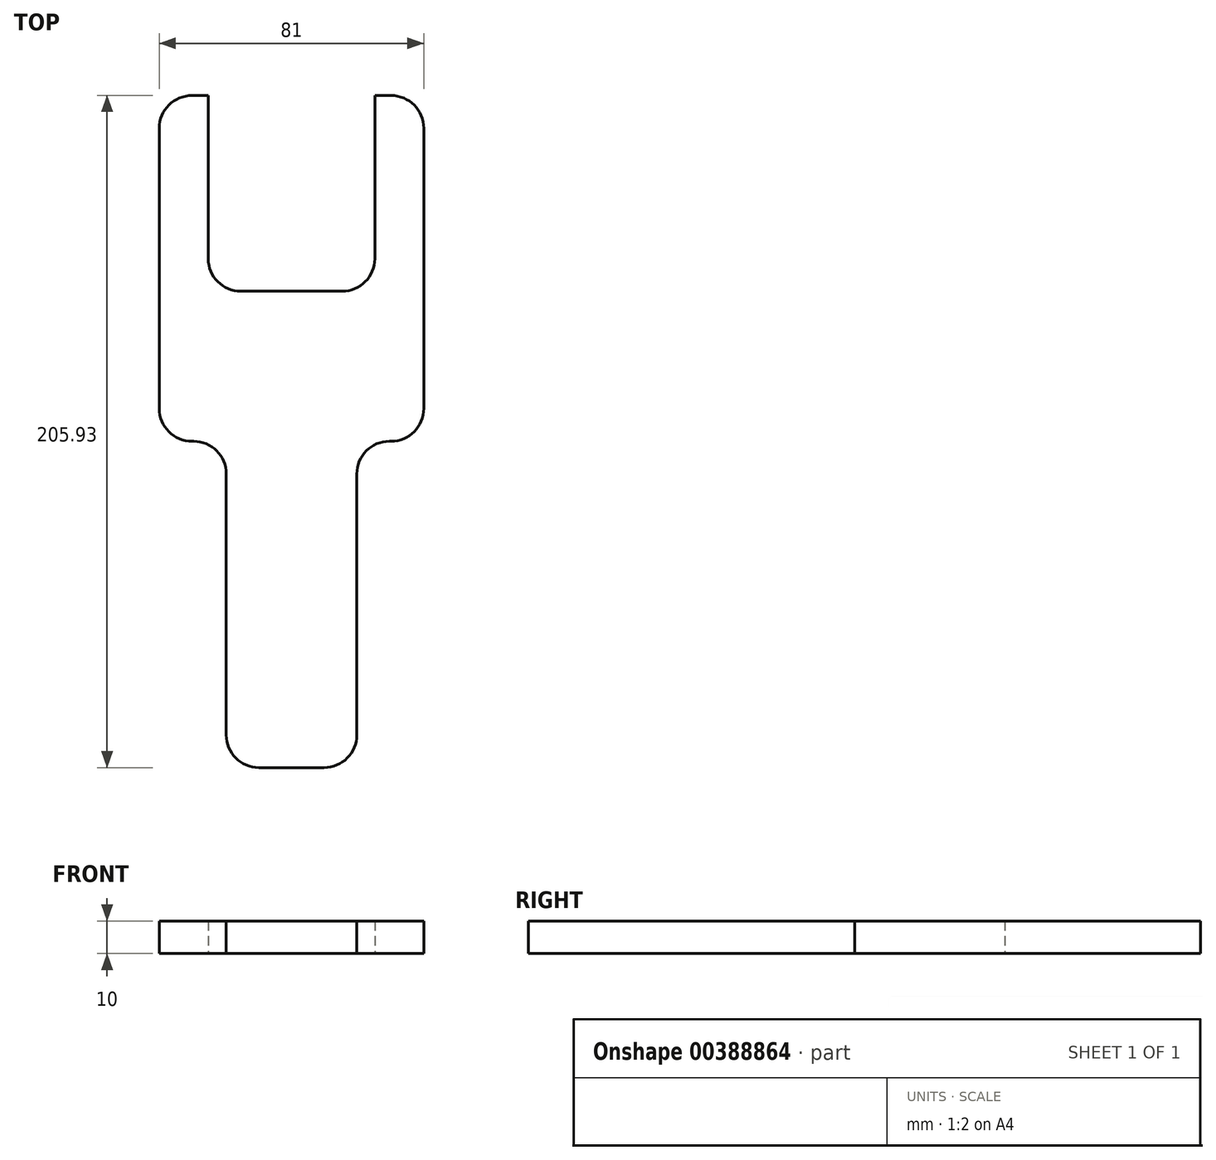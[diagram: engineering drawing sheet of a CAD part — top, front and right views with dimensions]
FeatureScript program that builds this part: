
annotation { "Feature Type Name" : "Feature", "Feature Type Description" : "" }
export const myFeature = defineFeature(function(context is Context, id is Id, definition is map)
    precondition{}
    {
        {
            var Q0;
            Q0=qCreatedBy(makeId("Top.planeOp"),FACE);
            var sketch = newSketch(context, id + "F0", { "sketchPlane" : qUnion([Q0])});
            skLineSegment(sketch, "E0", {"start": v(0, 87.3) * mm, "end": v(0, -159.9) * mm, "construction": true});
            skLineSegment(sketch, "E1", {"start": v(69.17, 0) * mm, "end": v(-67.83, 0) * mm, "construction": true});
            skLineSegment(sketch, "E2", {"start": v(25.5, 60) * mm, "end": v(25.5, 0) * mm});
            skLineSegment(sketch, "E3", {"start": v(25.5, 0) * mm, "end": v(0, 0) * mm});
            skLineSegment(sketch, "E4", {"start": v(25.5, 60) * mm, "end": v(40.5, 60) * mm});
            skLineSegment(sketch, "E5", {"start": v(40.5, 60) * mm, "end": v(40.5, -45.93) * mm});
            skLineSegment(sketch, "E6", {"start": v(40.5, -45.93) * mm, "end": v(20, -45.93) * mm});
            skLineSegment(sketch, "E7", {"start": v(20, -45.93) * mm, "end": v(20, -145.93) * mm});
            skLineSegment(sketch, "E8", {"start": v(20, -145.93) * mm, "end": v(0, -145.93) * mm});
            skLineSegment(sketch, "E9.MirrorCS", {"start": v(-25.5, 0) * mm, "end": v(0, 0) * mm});
            skLineSegment(sketch, "E10.MirrorCS", {"start": v(-25.5, 60) * mm, "end": v(-25.5, 0) * mm});
            skLineSegment(sketch, "E11.MirrorCS", {"start": v(-40.5, 60) * mm, "end": v(-40.5, -45.93) * mm});
            skLineSegment(sketch, "E12.MirrorCS", {"start": v(-40.5, -45.93) * mm, "end": v(-20, -45.93) * mm});
            skLineSegment(sketch, "E13.MirrorCS", {"start": v(-20, -45.93) * mm, "end": v(-20, -145.93) * mm});
            skLineSegment(sketch, "E14.MirrorCS", {"start": v(-20, -145.93) * mm, "end": v(0, -145.93) * mm});
            skLineSegment(sketch, "E15.MirrorCS", {"start": v(-25.5, 60) * mm, "end": v(-40.5, 60) * mm});
            skSolve(sketch);
        }
        {
            var Q0;
            Q0 = qSketchRegion(id + "F0", true);
            extrude(context, id + "F1", {"entities" : qUnion([Q0]), "depth" : 10 * mm});
        }
        {
            var Q0;
            Q0=makeQuery(id+"F1.opExtrude","SWEPT_EDGE",EDGE,{"disambiguationData":[OSD([sQuery(id+"F0.wireOp",EDGE,"E7"),sQuery(id+"F0.wireOp",EDGE,"E8")])]});
            var Q1;
            Q1=makeQuery(id+"F1.opExtrude","SWEPT_EDGE",EDGE,{"disambiguationData":[OSD([sQuery(id+"F0.wireOp",EDGE,"E13.MirrorCS"),sQuery(id+"F0.wireOp",EDGE,"E14.MirrorCS")])]});
            var Q2;
            Q2=makeQuery(id+"F1.opExtrude","SWEPT_EDGE",EDGE,{"disambiguationData":[OSD([sQuery(id+"F0.wireOp",EDGE,"E5"),sQuery(id+"F0.wireOp",EDGE,"E6")])]});
            var Q3;
            Q3=makeQuery(id+"F1.opExtrude","SWEPT_EDGE",EDGE,{"disambiguationData":[OSD([sQuery(id+"F0.wireOp",EDGE,"E6"),sQuery(id+"F0.wireOp",EDGE,"E7")])]});
            var Q4;
            Q4=makeQuery(id+"F1.opExtrude","SWEPT_EDGE",EDGE,{"disambiguationData":[OSD([sQuery(id+"F0.wireOp",EDGE,"E11.MirrorCS"),sQuery(id+"F0.wireOp",EDGE,"E12.MirrorCS")])]});
            var Q5;
            Q5=makeQuery(id+"F1.opExtrude","SWEPT_EDGE",EDGE,{"disambiguationData":[OSD([sQuery(id+"F0.wireOp",EDGE,"E12.MirrorCS"),sQuery(id+"F0.wireOp",EDGE,"E13.MirrorCS")])]});
            var Q6;
            Q6=makeQuery(id+"F1.opExtrude","SWEPT_EDGE",EDGE,{"disambiguationData":[OSD([sQuery(id+"F0.wireOp",EDGE,"E2"),sQuery(id+"F0.wireOp",EDGE,"E3")])]});
            var Q7;
            Q7=makeQuery(id+"F1.opExtrude","SWEPT_EDGE",EDGE,{"disambiguationData":[OSD([sQuery(id+"F0.wireOp",EDGE,"E9.MirrorCS"),sQuery(id+"F0.wireOp",EDGE,"E10.MirrorCS")])]});
            var Q8;
            Q8=makeQuery(id+"F1.opExtrude","SWEPT_EDGE",EDGE,{"disambiguationData":[OSD([sQuery(id+"F0.wireOp",EDGE,"E4"),sQuery(id+"F0.wireOp",EDGE,"E5")])]});
            var Q9;
            Q9=makeQuery(id+"F1.opExtrude","SWEPT_EDGE",EDGE,{"disambiguationData":[OSD([sQuery(id+"F0.wireOp",EDGE,"E11.MirrorCS"),sQuery(id+"F0.wireOp",EDGE,"E15.MirrorCS")])]});
            fillet(context, id + "F2", {"entities" : qUnion([Q0, Q1, Q2, Q3, Q4, Q5, Q6, Q7, Q8, Q9]), "radius" : 10 * mm, "tangentPropagation" : true, "allowEdgeOverflow" : false});
        }
    });
